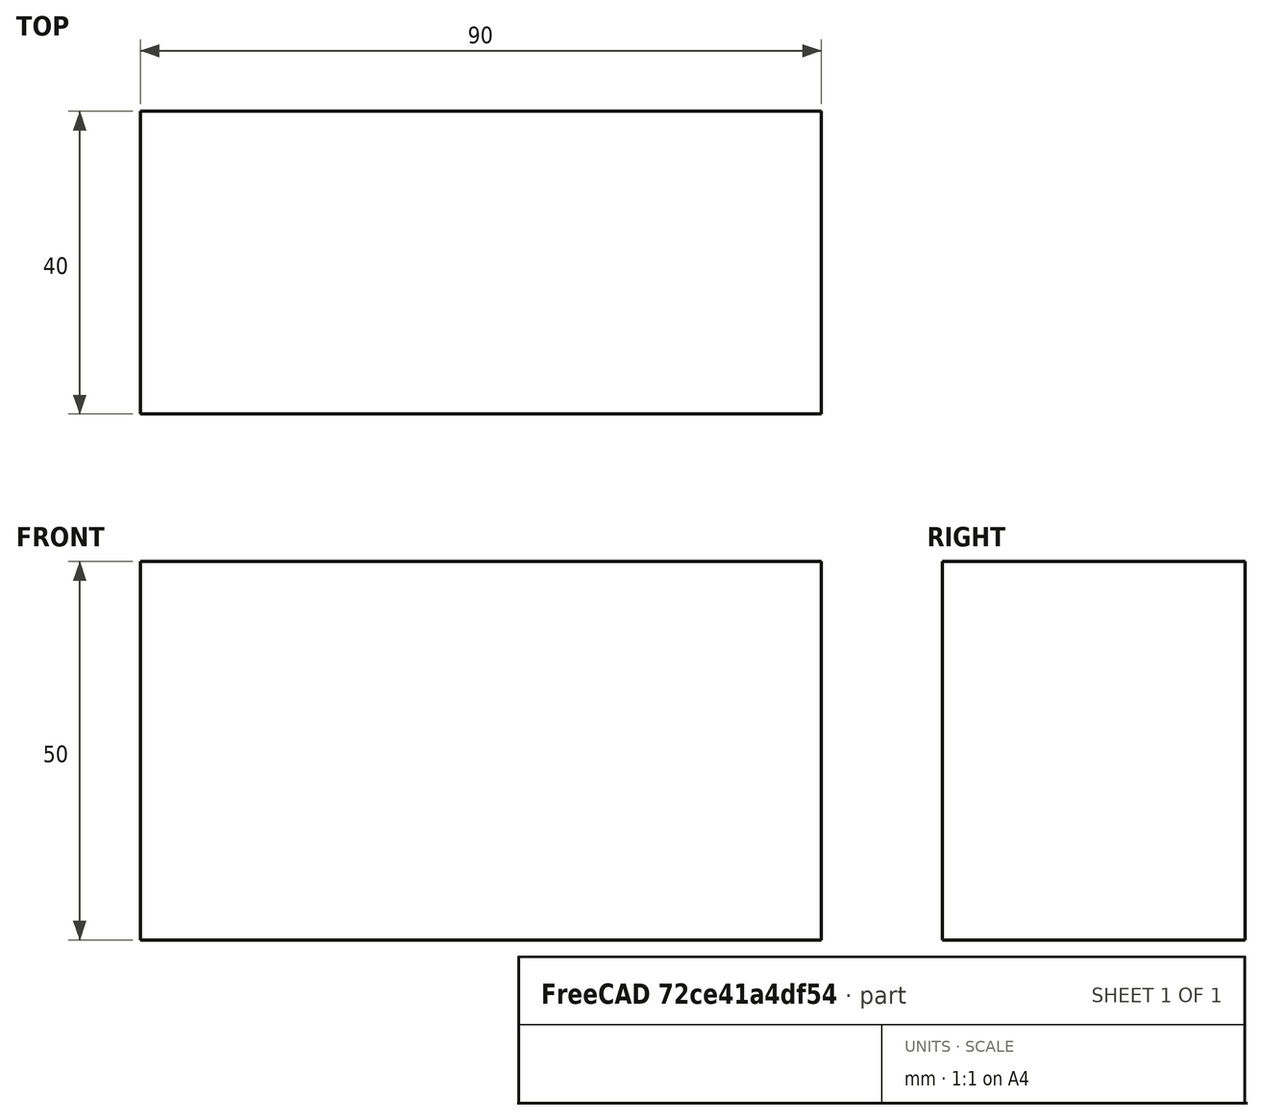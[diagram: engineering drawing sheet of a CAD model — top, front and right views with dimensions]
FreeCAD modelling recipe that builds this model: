
FCSTD DOCUMENT  (FreeCAD 0.15R4671 (Git))
Label: Flat Bar 90x40 EN10058 S235JR
License: All rights reserved
LicenseURL: http://en.wikipedia.org/wiki/All_rights_reserved
objects: Sketcher::SketchObject×1, Part::Extrusion×1
note: 2 computed .brp shape members not serialized (recipe doc carries the construction recipe); baked Part::Feature solids carry a one-line shape summary decoded from their .brp

FEATURE [Sketcher::SketchObject] Sketch
  sketch-geometry (4):
    g0: LineSegment StartX=-45 StartY=-20 StartZ=0 EndX=45 EndY=-20 EndZ=0
    g1: LineSegment StartX=45 StartY=-20 StartZ=0 EndX=45 EndY=20 EndZ=0
    g2: LineSegment StartX=45 StartY=20 StartZ=0 EndX=-45 EndY=20 EndZ=0
    g3: LineSegment StartX=-45 StartY=20 StartZ=0 EndX=-45 EndY=-20 EndZ=0
  constraints (12):
    c: Coincident(g0,g1)
    c: Coincident(g1,g2)
    c: Coincident(g2,g3)
    c: Coincident(g3,g0)
    c: Horizontal(g0)
    c: Horizontal(g2)
    c: Vertical(g1)
    c: Vertical(g3)
    c: Symmetric(g1,g2,g-2)
    c: Symmetric(g0,g1,g-1)
    c: DistanceY(g1) = 40
    c: DistanceX(g0) = 90
FEATURE [Part::Extrusion] Extrude  label="Flat Bar 90x40 EN10058 S235JR"
  Base = -> Sketch
  Dir = (0,0,50)
  Solid = true
